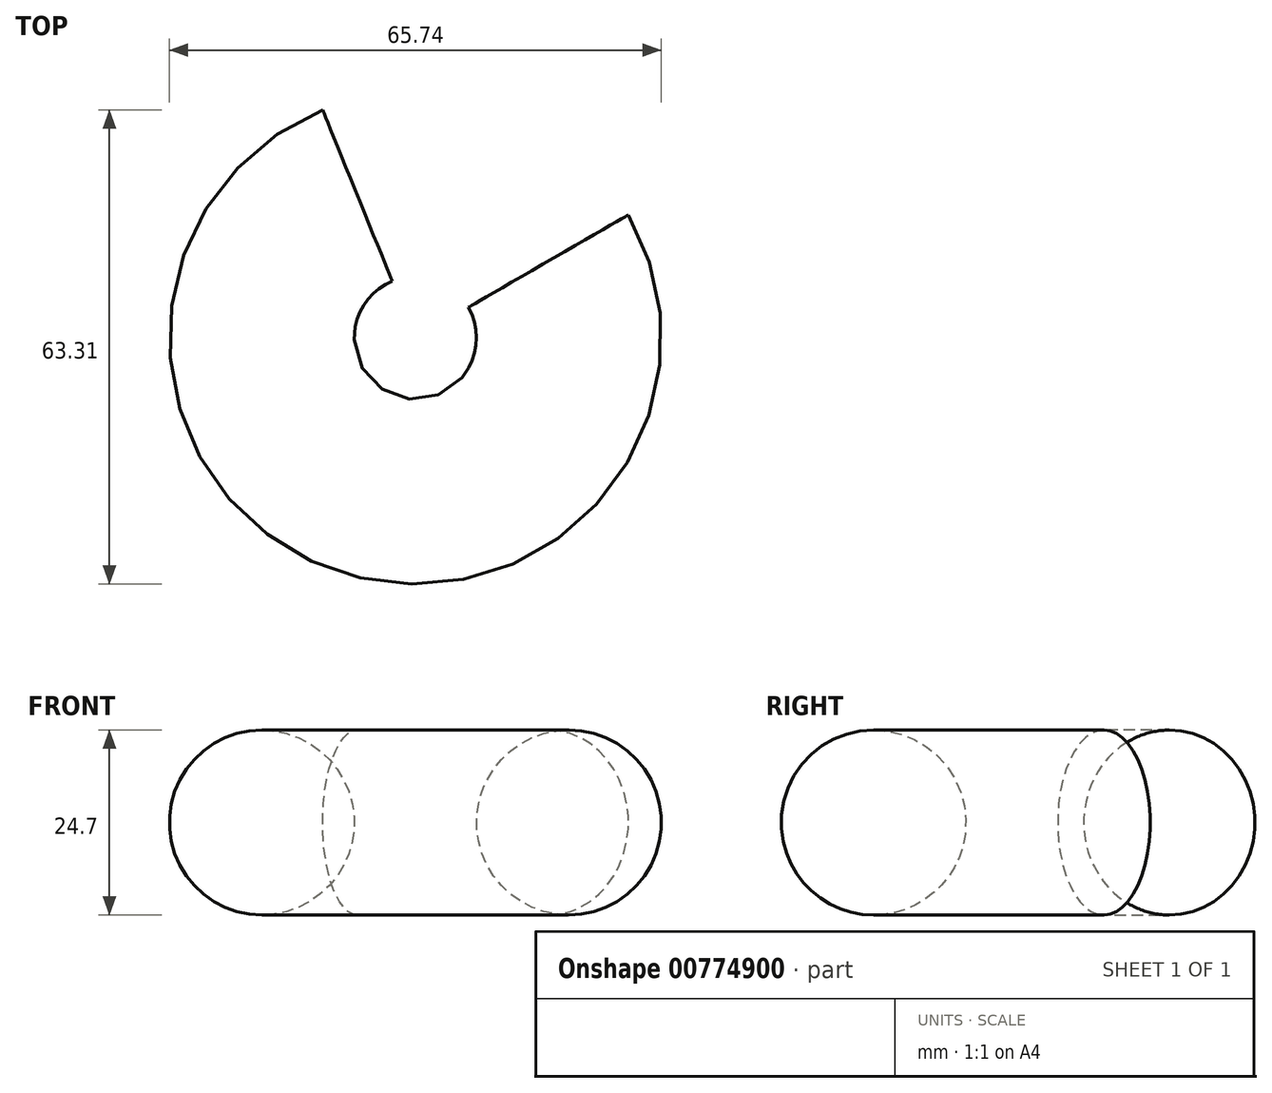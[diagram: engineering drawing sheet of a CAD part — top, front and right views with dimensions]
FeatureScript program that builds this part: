
annotation { "Feature Type Name" : "Feature", "Feature Type Description" : "" }
export const myFeature = defineFeature(function(context is Context, id is Id, definition is map)
    precondition{}
    {
        {
            var Q0;
            Q0=qCreatedBy(makeId("Front.planeOp"),FACE);
            var sketch = newSketch(context, id + "F0", { "sketchPlane" : qUnion([Q0])});
            skCircle(sketch, "E0", {"center": v(20.52, 0) * mm, "radius": 12.35 * mm});
            skLineSegment(sketch, "E1", {"start": v(0, -15.9) * mm, "end": v(0, 26) * mm});
            skSolve(sketch);
        }
        {
            var Q0;
            Q0=makeQuery(id+"F0.imprint","IMPRINT",FACE,{"disambiguationData":[TD([[makeQuery(id+"F0.imprint","IMPRINT",EDGE,{"derivedFrom":sQuery(id+"F0.wireOp",EDGE,"E0")}),1.0]])]});
            var Q1;
            Q1=sQuery(id+"F0.wireOp",EDGE,"E1");
            revolve(context, id + "F1", {"surfaceOperationType" : NewSurfaceOperationType.NEW, "entities" : qUnion([Q0]), "axis" : qUnion([Q1]), "revolveType" : RevolveType.TWO_DIRECTIONS, "angle" : 30 * degree, "angleBack" : 112.15 * degree});
        }
    });
